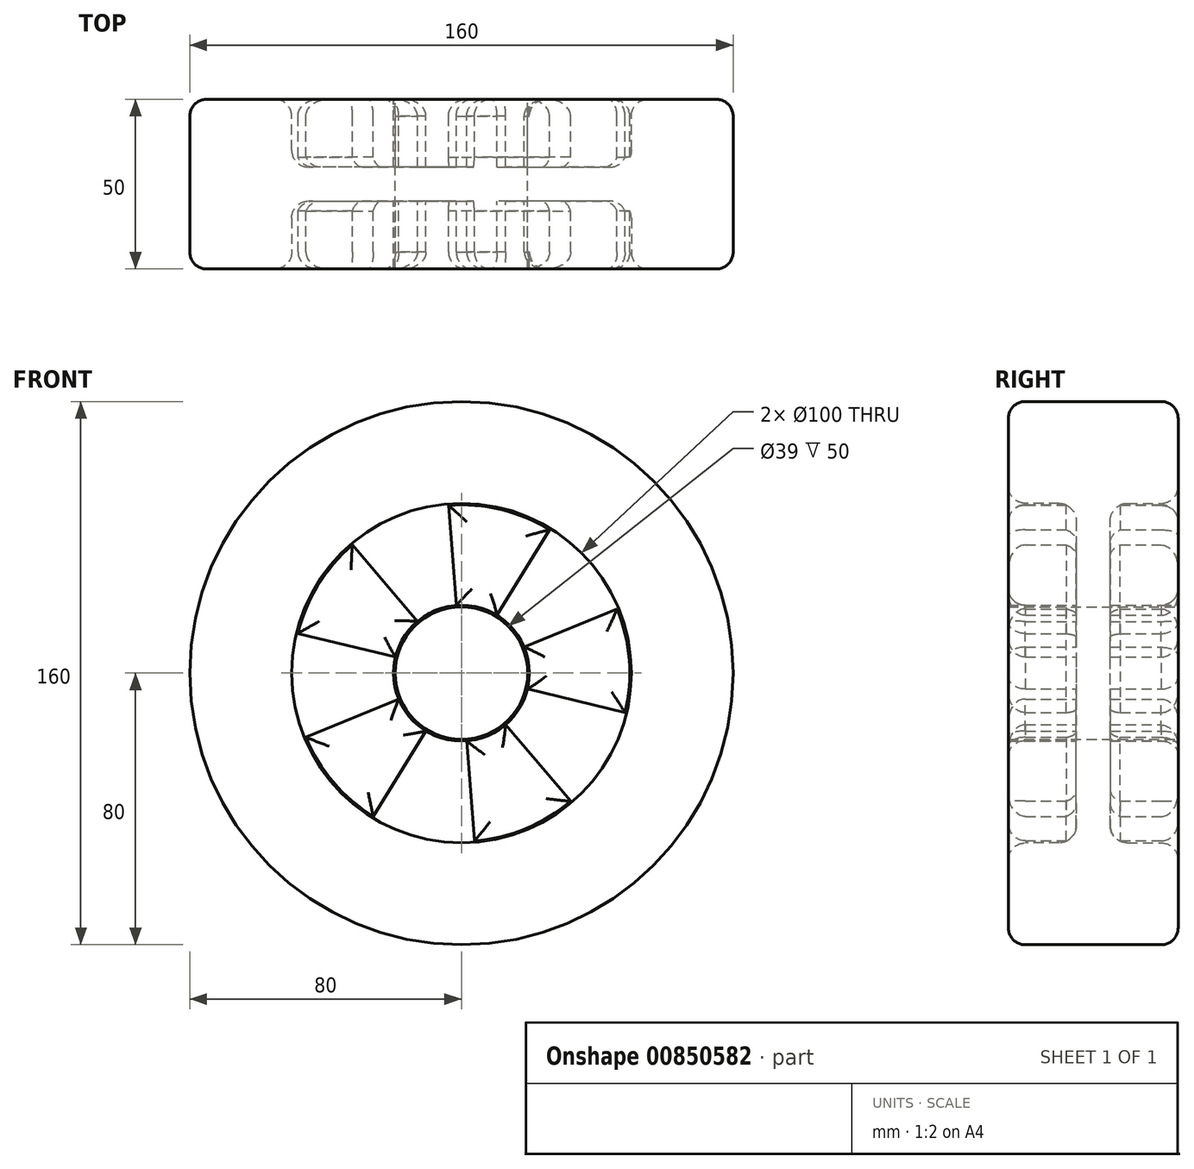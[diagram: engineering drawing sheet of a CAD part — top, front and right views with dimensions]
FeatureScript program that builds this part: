
annotation { "Feature Type Name" : "Feature", "Feature Type Description" : "" }
export const myFeature = defineFeature(function(context is Context, id is Id, definition is map)
    precondition{}
    {
        {
            var Q0;
            Q0=qCreatedBy(makeId("Front.planeOp"),FACE);
            var sketch = newSketch(context, id + "F0", { "sketchPlane" : qUnion([Q0])});
            skCircle(sketch, "E0", {"center": v(0, 0) * mm, "radius": 80 * mm});
            skSolve(sketch);
        }
        {
            var Q0;
            Q0=makeQuery(id+"F0.imprint","IMPRINT",FACE,{"disambiguationData":[TD([[makeQuery(id+"F0.imprint","IMPRINT",EDGE,{"derivedFrom":sQuery(id+"F0.wireOp",EDGE,"E0")}),1.0]])]});
            extrude(context, id + "F1", {"entities" : qUnion([Q0]), "depth" : 50 * mm, "offsetDistance" : 25 * mm});
        }
        {
            var Q0;
            Q0=makeQuery(id+"F1.opExtrude","CAP_FACE",FACE,{"disambiguationData":[OSD([sQuery(id+"F0.wireOp",EDGE,"E0")])],"isStart":false});
            var sketch = newSketch(context, id + "F2", { "sketchPlane" : qUnion([Q0])});
            skPoint(sketch, "E1", {"position": v(0, 0) * mm});
            skCircle(sketch, "E2", {"center": v(0, 0) * mm, "radius": 50 * mm});
            skSolve(sketch);
        }
        {
            var Q0;
            Q0 = qSketchRegion(id + "F2", true);
            extrude(context, id + "F3", {"entities" : qUnion([Q0]), "operationType" : NewBodyOperationType.REMOVE, "oppositeDirection" : true, "depth" : 20 * mm, "offsetDistance" : 25 * mm});
        }
        {
            var Q0;
            Q0=makeQuery(id+"F1.opExtrude","CAP_FACE",FACE,{"disambiguationData":[OSD([sQuery(id+"F0.wireOp",EDGE,"E0")])],"isStart":false});
            var Q1;
            Q1=makeQuery(id+"F3.boolean.opBoolean","COPY",FACE,{"derivedFrom":makeQuery(id+"F3.opExtrude","CAP_FACE",FACE,{"disambiguationData":[OSD([sQuery(id+"F2.wireOp",EDGE,"E2")])],"isStart":false})});
            fillet(context, id + "F4", {"entities" : qUnion([Q0, Q1]), "radius" : 5 * mm, "tangentPropagation" : true, "allowEdgeOverflow" : false});
        }
        {
            var Q0;
            Q0=makeQuery(id+"F1.opExtrude","CAP_FACE",FACE,{"disambiguationData":[OSD([sQuery(id+"F0.wireOp",EDGE,"E0")])],"isStart":true});
            var sketch = newSketch(context, id + "F5", { "sketchPlane" : qUnion([Q0])});
            skCircle(sketch, "E3", {"center": v(0, 0) * mm, "radius": 50 * mm});
            skSolve(sketch);
        }
        {
            var Q0;
            Q0=makeQuery(id+"F5.imprint","IMPRINT",FACE,{"disambiguationData":[TD([[makeQuery(id+"F5.imprint","IMPRINT",EDGE,{"derivedFrom":sQuery(id+"F5.wireOp",EDGE,"E3")}),1.0]])]});
            extrude(context, id + "F6", {"entities" : qUnion([Q0]), "operationType" : NewBodyOperationType.REMOVE, "oppositeDirection" : true, "depth" : 20 * mm, "offsetDistance" : 25 * mm});
        }
        {
            var Q0;
            Q0=makeQuery(id+"F1.opExtrude","CAP_FACE",FACE,{"disambiguationData":[OSD([sQuery(id+"F0.wireOp",EDGE,"E0")])],"isStart":true});
            var Q1;
            Q1=makeQuery(id+"F6.boolean.opBoolean","COPY",EDGE,{"derivedFrom":makeQuery(id+"F6.opExtrude","CAP_EDGE",EDGE,{"disambiguationData":[OSD([sQuery(id+"F5.wireOp",EDGE,"E3")])],"isStart":true})});
            var Q2;
            Q2=makeQuery(id+"F6.boolean.opBoolean","COPY",EDGE,{"derivedFrom":makeQuery(id+"F6.opExtrude","CAP_EDGE",EDGE,{"disambiguationData":[OSD([sQuery(id+"F5.wireOp",EDGE,"E3")])],"isStart":false})});
            fillet(context, id + "F7", {"entities" : qUnion([Q0, Q1, Q2]), "radius" : 5 * mm, "tangentPropagation" : true, "allowEdgeOverflow" : false});
        }
        {
            var Q0;
            Q0=makeQuery(id+"F6.boolean.opBoolean","COPY",FACE,{"derivedFrom":makeQuery(id+"F6.opExtrude","CAP_FACE",FACE,{"disambiguationData":[OSD([sQuery(id+"F5.wireOp",EDGE,"E3")])],"isStart":false})});
            var sketch = newSketch(context, id + "F8", { "sketchPlane" : qUnion([Q0])});
            skCircle(sketch, "E4", {"center": v(0, 0) * mm, "radius": 20 * mm});
            skSolve(sketch);
        }
        {
            var Q0;
            Q0=makeQuery(id+"F8.imprint","IMPRINT",FACE,{"disambiguationData":[TD([[makeQuery(id+"F8.imprint","IMPRINT",EDGE,{"derivedFrom":sQuery(id+"F8.wireOp",EDGE,"E4")}),1.0]])]});
            extrude(context, id + "F9", {"entities" : qUnion([Q0]), "operationType" : NewBodyOperationType.REMOVE, "endBound" : BoundingType.UP_TO_NEXT, "oppositeDirection" : true, "depth" : 25 * mm, "offsetDistance" : 25 * mm});
        }
        {
            var Q0;
            Q0=makeQuery(id+"F1.opExtrude","CAP_FACE",FACE,{"disambiguationData":[OSD([sQuery(id+"F0.wireOp",EDGE,"E0")])],"isStart":true});
            var sketch = newSketch(context, id + "F10", { "sketchPlane" : qUnion([Q0])});
            skCircle(sketch, "E5", {"center": v(0, 0) * mm, "radius": 49.55 * mm});
            skLineSegment(sketch, "E6", {"start": v(1.54, 19.94) * mm, "end": v(3.82, 49.4) * mm});
            skLineSegment(sketch, "E7.1.0", {"start": v(-10.47, 17.04) * mm, "end": v(-25.95, 42.21) * mm});
            skLineSegment(sketch, "E7.2.0", {"start": v(-18.49, 7.63) * mm, "end": v(-45.8, 18.9) * mm});
            skLineSegment(sketch, "E7.3.0", {"start": v(-19.44, -4.7) * mm, "end": v(-48.16, -11.63) * mm});
            skLineSegment(sketch, "E7.4.0", {"start": v(-12.97, -15.23) * mm, "end": v(-32.13, -37.72) * mm});
            skLineSegment(sketch, "E7.5.0", {"start": v(-1.54, -19.94) * mm, "end": v(-3.82, -49.4) * mm});
            skLineSegment(sketch, "E7.6.0", {"start": v(10.47, -17.04) * mm, "end": v(25.95, -42.21) * mm});
            skLineSegment(sketch, "E7.7.0", {"start": v(18.49, -7.63) * mm, "end": v(45.8, -18.9) * mm});
            skLineSegment(sketch, "E7.8.0", {"start": v(19.44, 4.7) * mm, "end": v(48.16, 11.63) * mm});
            skLineSegment(sketch, "E7.9.0", {"start": v(12.97, 15.23) * mm, "end": v(32.13, 37.72) * mm});
            skCircle(sketch, "E8", {"center": v(0, 0) * mm, "radius": 20 * mm});
            skSolve(sketch);
        }
        {
            var Q0;
            {var subQ0=sQuery(id+"F10.wireOp",EDGE,"E7.4.0");Q0=makeQuery(id+"F10.imprint","IMPRINT",FACE,{"disambiguationData":[TD([[makeQuery(id+"F10.imprint","IMPRINT",EDGE,{"derivedFrom":subQ0}),1.0]])]});}
            var Q1;
            {var subQ0=sQuery(id+"F10.wireOp",EDGE,"E7.2.0");Q1=makeQuery(id+"F10.imprint","IMPRINT",FACE,{"disambiguationData":[TD([[makeQuery(id+"F10.imprint","IMPRINT",EDGE,{"derivedFrom":subQ0}),1.0]])]});}
            var Q2;
            {var subQ0=sQuery(id+"F10.wireOp",EDGE,"E6");Q2=makeQuery(id+"F10.imprint","IMPRINT",FACE,{"disambiguationData":[TD([[makeQuery(id+"F10.imprint","IMPRINT",EDGE,{"derivedFrom":subQ0}),1.0]])]});}
            var Q3;
            {var subQ0=sQuery(id+"F10.wireOp",EDGE,"E7.8.0");Q3=makeQuery(id+"F10.imprint","IMPRINT",FACE,{"disambiguationData":[TD([[makeQuery(id+"F10.imprint","IMPRINT",EDGE,{"derivedFrom":subQ0}),1.0]])]});}
            var Q4;
            {var subQ0=sQuery(id+"F10.wireOp",EDGE,"E7.6.0");Q4=makeQuery(id+"F10.imprint","IMPRINT",FACE,{"disambiguationData":[TD([[makeQuery(id+"F10.imprint","IMPRINT",EDGE,{"derivedFrom":subQ0}),1.0]])]});}
            extrude(context, id + "F11", {"entities" : qUnion([Q0, Q1, Q2, Q3, Q4]), "operationType" : NewBodyOperationType.ADD, "oppositeDirection" : true, "depth" : 50 * mm, "offsetDistance" : 25 * mm});
        }
        {
            var Q0;
            Q0=makeQuery(id+"F11.opExtrude","CAP_FACE",FACE,{"disambiguationData":[OSD([sQuery(id+"F10.wireOp",EDGE,"E5"),sQuery(id+"F10.wireOp",EDGE,"E6"),sQuery(id+"F10.wireOp",EDGE,"E7.1.0"),sQuery(id+"F10.wireOp",EDGE,"NeFTXqSq-kob4-ibFe-W7Cx-cGxDp6ZRejmO")])],"isStart":true});
            var Q1;
            Q1=makeQuery(id+"F11.opExtrude","CAP_FACE",FACE,{"disambiguationData":[OSD([sQuery(id+"F10.wireOp",EDGE,"E5"),sQuery(id+"F10.wireOp",EDGE,"E7.8.0"),sQuery(id+"F10.wireOp",EDGE,"E7.9.0"),sQuery(id+"F10.wireOp",EDGE,"NeFTXqSq-kob4-ibFe-W7Cx-cGxDp6ZRejmO")])],"isStart":true});
            var Q2;
            Q2=makeQuery(id+"F11.opExtrude","CAP_FACE",FACE,{"disambiguationData":[OSD([sQuery(id+"F10.wireOp",EDGE,"E5"),sQuery(id+"F10.wireOp",EDGE,"E7.6.0"),sQuery(id+"F10.wireOp",EDGE,"E7.7.0"),sQuery(id+"F10.wireOp",EDGE,"NeFTXqSq-kob4-ibFe-W7Cx-cGxDp6ZRejmO")])],"isStart":true});
            var Q3;
            Q3=makeQuery(id+"F11.opExtrude","CAP_FACE",FACE,{"disambiguationData":[OSD([sQuery(id+"F10.wireOp",EDGE,"E5"),sQuery(id+"F10.wireOp",EDGE,"E7.2.0"),sQuery(id+"F10.wireOp",EDGE,"E7.3.0"),sQuery(id+"F10.wireOp",EDGE,"NeFTXqSq-kob4-ibFe-W7Cx-cGxDp6ZRejmO")])],"isStart":true});
            var Q4;
            Q4=makeQuery(id+"F11.opExtrude","CAP_FACE",FACE,{"disambiguationData":[OSD([sQuery(id+"F10.wireOp",EDGE,"E5"),sQuery(id+"F10.wireOp",EDGE,"E7.4.0"),sQuery(id+"F10.wireOp",EDGE,"E7.5.0"),sQuery(id+"F10.wireOp",EDGE,"NeFTXqSq-kob4-ibFe-W7Cx-cGxDp6ZRejmO")])],"isStart":true});
            fillet(context, id + "F12", {"entities" : qUnion([Q0, Q1, Q2, Q3, Q4]), "radius" : 5 * mm, "tangentPropagation" : true, "allowEdgeOverflow" : false});
        }
        {
            var Q0;
            Q0=makeQuery(id+"F11.opExtrude","CAP_FACE",FACE,{"disambiguationData":[OSD([sQuery(id+"F10.wireOp",EDGE,"E5"),sQuery(id+"F10.wireOp",EDGE,"E7.4.0"),sQuery(id+"F10.wireOp",EDGE,"E7.5.0"),sQuery(id+"F10.wireOp",EDGE,"NeFTXqSq-kob4-ibFe-W7Cx-cGxDp6ZRejmO")])],"isStart":false});
            var Q1;
            Q1=makeQuery(id+"F11.opExtrude","CAP_FACE",FACE,{"disambiguationData":[OSD([sQuery(id+"F10.wireOp",EDGE,"E5"),sQuery(id+"F10.wireOp",EDGE,"E7.6.0"),sQuery(id+"F10.wireOp",EDGE,"E7.7.0"),sQuery(id+"F10.wireOp",EDGE,"NeFTXqSq-kob4-ibFe-W7Cx-cGxDp6ZRejmO")])],"isStart":false});
            var Q2;
            Q2=makeQuery(id+"F11.opExtrude","CAP_EDGE",EDGE,{"disambiguationData":[OSD([sQuery(id+"F10.wireOp",EDGE,"E7.2.0")])],"isStart":false});
            var Q3;
            Q3=makeQuery(id+"F11.opExtrude","CAP_FACE",FACE,{"disambiguationData":[OSD([sQuery(id+"F10.wireOp",EDGE,"E5"),sQuery(id+"F10.wireOp",EDGE,"E6"),sQuery(id+"F10.wireOp",EDGE,"E7.1.0"),sQuery(id+"F10.wireOp",EDGE,"NeFTXqSq-kob4-ibFe-W7Cx-cGxDp6ZRejmO")])],"isStart":false});
            var Q4;
            Q4=makeQuery(id+"F11.opExtrude","CAP_FACE",FACE,{"disambiguationData":[OSD([sQuery(id+"F10.wireOp",EDGE,"E5"),sQuery(id+"F10.wireOp",EDGE,"E7.8.0"),sQuery(id+"F10.wireOp",EDGE,"E7.9.0"),sQuery(id+"F10.wireOp",EDGE,"NeFTXqSq-kob4-ibFe-W7Cx-cGxDp6ZRejmO")])],"isStart":false});
            var Q5;
            Q5=makeQuery(id+"F11.opExtrude","CAP_FACE",FACE,{"disambiguationData":[OSD([sQuery(id+"F10.wireOp",EDGE,"E5"),sQuery(id+"F10.wireOp",EDGE,"E7.2.0"),sQuery(id+"F10.wireOp",EDGE,"E7.3.0"),sQuery(id+"F10.wireOp",EDGE,"NeFTXqSq-kob4-ibFe-W7Cx-cGxDp6ZRejmO")])],"isStart":false});
            fillet(context, id + "F13", {"entities" : qUnion([Q0, Q1, Q2, Q3, Q4, Q5]), "radius" : 5 * mm, "tangentPropagation" : true, "allowEdgeOverflow" : false});
        }
        {
            var Q0;
            Q0=makeQuery(id+"F1.opExtrude","CAP_FACE",FACE,{"disambiguationData":[OSD([sQuery(id+"F0.wireOp",EDGE,"E0")])],"isStart":true});
            var sketch = newSketch(context, id + "F14", { "sketchPlane" : qUnion([Q0])});
            skCircle(sketch, "E9", {"center": v(0, 0) * mm, "radius": 19.5 * mm});
            skCircle(sketch, "E10", {"center": v(0, 0) * mm, "radius": 20 * mm});
            skSolve(sketch);
        }
        {
            var Q0;
            Q0=makeQuery(id+"F14.imprint","IMPRINT",FACE,{"disambiguationData":[TD([[makeQuery(id+"F14.imprint","IMPRINT",EDGE,{"derivedFrom":sQuery(id+"F14.wireOp",EDGE,"E9")}),-1.0]])]});
            extrude(context, id + "F15", {"entities" : qUnion([Q0]), "operationType" : NewBodyOperationType.ADD, "oppositeDirection" : true, "depth" : 50 * mm, "offsetDistance" : 25 * mm});
        }
        {
            var Q0;
            Q0=qCreatedBy(makeId("Top.planeOp"),FACE);
            cPlane(context, id + "F16", {"entities" : qUnion([Q0]), "cplaneType" : CPlaneType.OFFSET, "offset" : 75 * mm, "width" : 150 * mm, "height" : 150 * mm});
        }
    });
